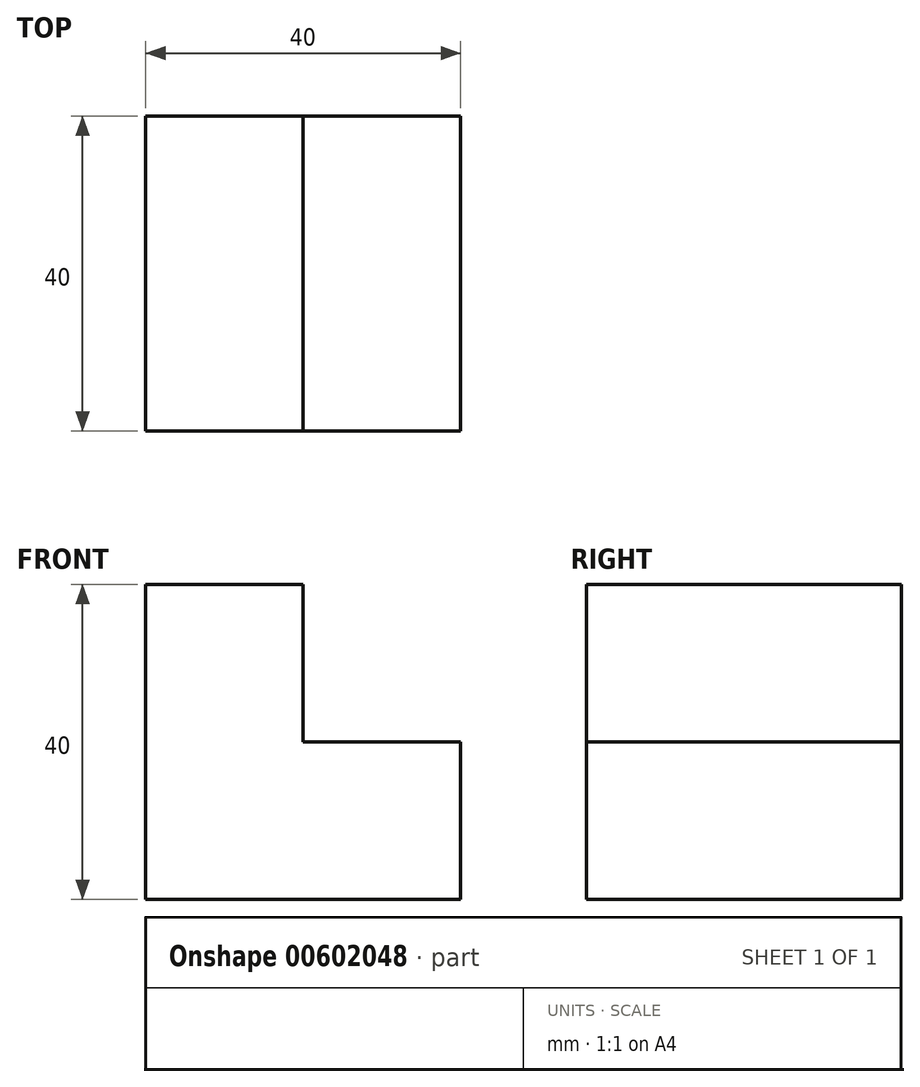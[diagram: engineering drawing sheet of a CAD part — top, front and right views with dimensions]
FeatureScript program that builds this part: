
annotation { "Feature Type Name" : "Feature", "Feature Type Description" : "" }
export const myFeature = defineFeature(function(context is Context, id is Id, definition is map)
    precondition{}
    {
        {
            var Q0;
            Q0=qCreatedBy(makeId("Front.planeOp"),FACE);
            var sketch = newSketch(context, id + "F0", { "sketchPlane" : qUnion([Q0])});
            skLineSegment(sketch, "E0", {"start": v(-36.1, 41.54) * mm, "end": v(-36.1, 1.54) * mm});
            skLineSegment(sketch, "E1", {"start": v(-36.1, 1.54) * mm, "end": v(3.9, 1.54) * mm});
            skLineSegment(sketch, "E2", {"start": v(3.9, 1.54) * mm, "end": v(3.9, 21.54) * mm});
            skLineSegment(sketch, "E3", {"start": v(3.9, 21.54) * mm, "end": v(-16.1, 21.54) * mm});
            skLineSegment(sketch, "E4", {"start": v(-16.1, 21.54) * mm, "end": v(-16.1, 41.54) * mm});
            skLineSegment(sketch, "E5", {"start": v(-16.1, 41.54) * mm, "end": v(-36.1, 41.54) * mm});
            skSolve(sketch);
        }
        {
            var Q0;
            Q0 = qSketchRegion(id + "F0", true);
            extrude(context, id + "F1", {"entities" : qUnion([Q0]), "depth" : 40 * mm, "offsetDistance" : 25 * mm});
        }
    });
